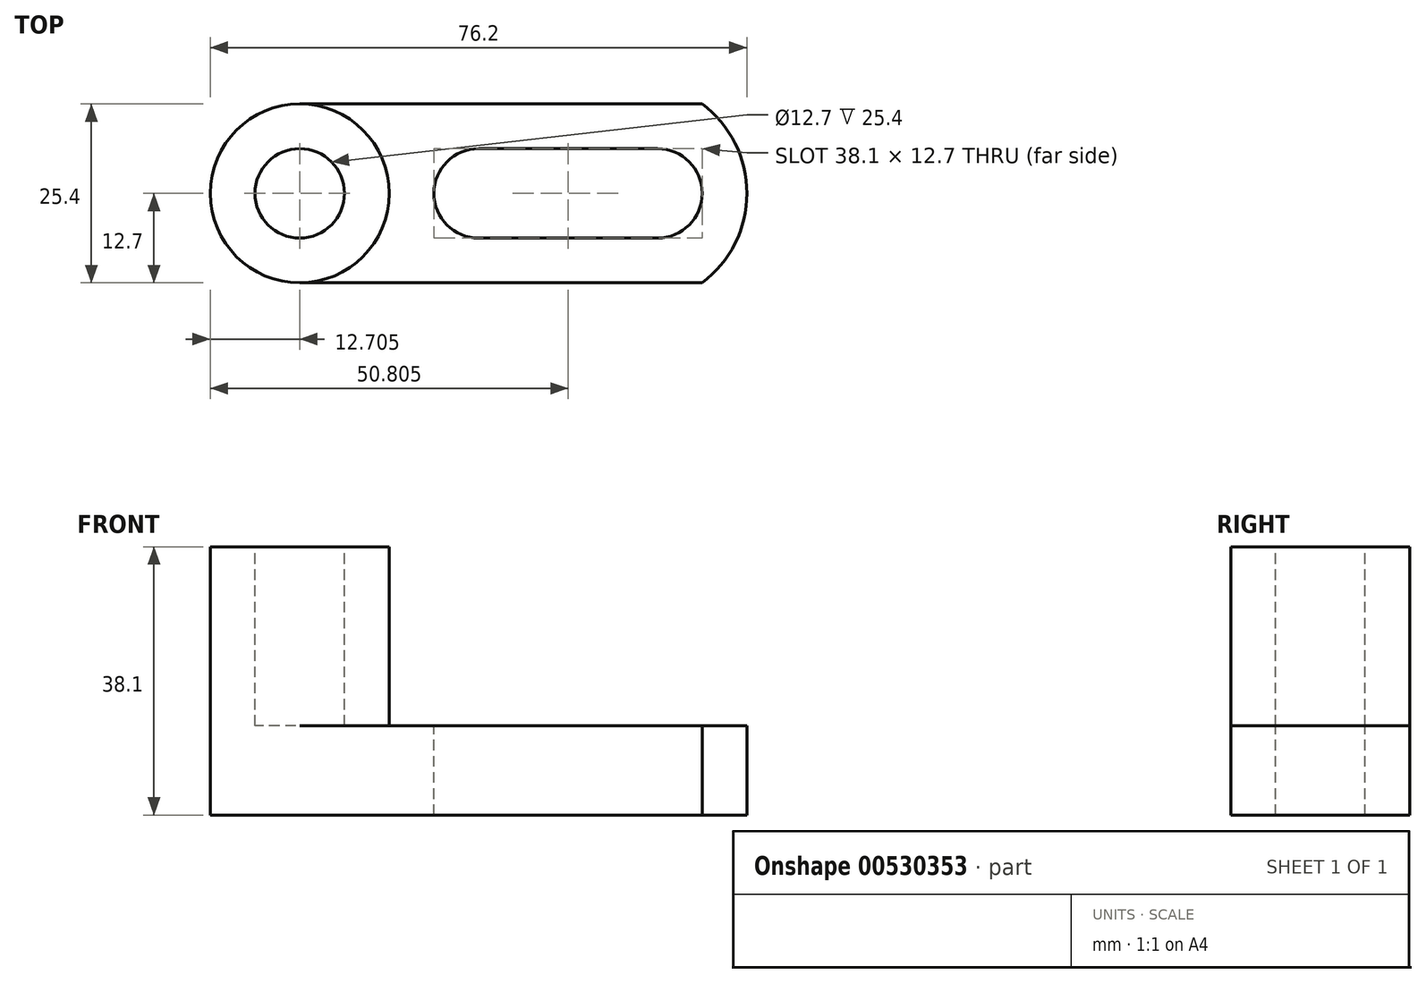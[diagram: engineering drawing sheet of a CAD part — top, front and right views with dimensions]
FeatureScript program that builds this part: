
annotation { "Feature Type Name" : "Feature", "Feature Type Description" : "" }
export const myFeature = defineFeature(function(context is Context, id is Id, definition is map)
    precondition{}
    {
        {
            var Q0;
            Q0=qCreatedBy(makeId("Front.planeOp"),FACE);
            var sketch = newSketch(context, id + "F0", { "sketchPlane" : qUnion([Q0])});
            skLineSegment(sketch, "E0", {"start": v(-50.57, 38.1) * mm, "end": v(-50.57, 0) * mm});
            skLineSegment(sketch, "E1", {"start": v(-50.57, 0) * mm, "end": v(25.63, 0) * mm});
            skLineSegment(sketch, "E2", {"start": v(25.63, 0) * mm, "end": v(25.63, 12.7) * mm});
            skLineSegment(sketch, "E3", {"start": v(25.63, 12.7) * mm, "end": v(-25.17, 12.7) * mm});
            skLineSegment(sketch, "E4", {"start": v(-25.17, 12.7) * mm, "end": v(-25.17, 38.1) * mm});
            skLineSegment(sketch, "E5", {"start": v(-25.17, 38.1) * mm, "end": v(-50.57, 38.1) * mm});
            skSolve(sketch);
        }
        {
            var Q0;
            Q0 = qSketchRegion(id + "F0", true);
            extrude(context, id + "F1", {"entities" : qUnion([Q0]), "depth" : 25.4 * mm, "offsetDistance" : 25.4 * mm});
        }
        {
            var Q0;
            Q0=makeQuery(id+"F1.opExtrude","SWEPT_FACE",FACE,{"disambiguationData":[OSD([sQuery(id+"F0.wireOp",EDGE,"E5")])]});
            var sketch = newSketch(context, id + "F2", { "sketchPlane" : qUnion([Q0])});
            skSolve(sketch);
        }
        {
            var Q0;
            {var subQ0=sQuery(id+"F0.wireOp",EDGE,"E5");Q0=makeQuery(id+"F2.imprint","IMPRINT",FACE,{"disambiguationData":[TD([[makeQuery(id+"F2.imprint","IMPRINT",EDGE,{"derivedFrom":makeQuery(id+"F1.opExtrude","CAP_EDGE",EDGE,{"disambiguationData":[OSD([subQ0])],"isStart":true})}),1.0]])]});}
            var sketch = newSketch(context, id + "F3", { "sketchPlane" : qUnion([Q0])});
            skCircle(sketch, "E6", {"center": v(-37.87, -12.7) * mm, "radius": 12.7 * mm});
            skSolve(sketch);
        }
        {
            var Q0;
            {var subQ0=sQuery(id+"F3.wireOp",EDGE,"E6");var subQ1=sQuery(id+"F0.wireOp",EDGE,"E5");var subQ2=makeQuery(id+"F2.imprint","IMPRINT",EDGE,{"derivedFrom":makeQuery(id+"F1.opExtrude","CAP_EDGE",EDGE,{"disambiguationData":[OSD([subQ1])],"isStart":true})});var subQ3=makeQuery(id+"F3.imprint","INTERSECT",VERTEX,{"derivedFrom":[subQ2,subQ0]});Q0=makeQuery(id+"F3.imprint","IMPRINT",FACE,{"disambiguationData":[TD([[makeQuery(id+"F3.imprint","IMPRINT",EDGE,{"disambiguationData":[TD([[subQ3,-1.0]])],"derivedFrom":subQ0}),-1.0]])]});}
            var Q1;
            {var subQ0=sQuery(id+"F3.wireOp",EDGE,"E6");var subQ1=sQuery(id+"F0.wireOp",EDGE,"E5");var subQ2=makeQuery(id+"F2.imprint","IMPRINT",EDGE,{"derivedFrom":makeQuery(id+"F1.opExtrude","CAP_EDGE",EDGE,{"disambiguationData":[OSD([subQ1])],"isStart":true})});var subQ3=makeQuery(id+"F3.imprint","INTERSECT",VERTEX,{"derivedFrom":[subQ2,subQ0]});Q1=makeQuery(id+"F3.imprint","IMPRINT",FACE,{"disambiguationData":[TD([[makeQuery(id+"F3.imprint","IMPRINT",EDGE,{"disambiguationData":[TD([[subQ3,1.0]])],"derivedFrom":subQ0}),-1.0]])]});}
            var Q2;
            {var subQ0=sQuery(id+"F3.wireOp",EDGE,"E6");var subQ1=sQuery(id+"F0.wireOp",EDGE,"E5");var subQ4=makeQuery(id+"F2.imprint","IMPRINT",EDGE,{"derivedFrom":makeQuery(id+"F1.opExtrude","CAP_EDGE",EDGE,{"disambiguationData":[OSD([subQ1])],"isStart":false})});var subQ5=makeQuery(id+"F3.imprint","INTERSECT",VERTEX,{"derivedFrom":[subQ4,subQ0]});Q2=makeQuery(id+"F3.imprint","IMPRINT",FACE,{"disambiguationData":[TD([[makeQuery(id+"F3.imprint","IMPRINT",EDGE,{"disambiguationData":[TD([[subQ5,1.0]])],"derivedFrom":subQ0}),-1.0]])]});}
            var Q3;
            {var subQ0=sQuery(id+"F3.wireOp",EDGE,"E6");var subQ1=sQuery(id+"F0.wireOp",EDGE,"E5");var subQ4=makeQuery(id+"F2.imprint","IMPRINT",EDGE,{"derivedFrom":makeQuery(id+"F1.opExtrude","CAP_EDGE",EDGE,{"disambiguationData":[OSD([subQ1])],"isStart":false})});var subQ5=makeQuery(id+"F3.imprint","INTERSECT",VERTEX,{"derivedFrom":[subQ4,subQ0]});Q3=makeQuery(id+"F3.imprint","IMPRINT",FACE,{"disambiguationData":[TD([[makeQuery(id+"F3.imprint","IMPRINT",EDGE,{"disambiguationData":[TD([[subQ5,-1.0]])],"derivedFrom":subQ0}),-1.0]])]});}
            extrude(context, id + "F4", {"entities" : qUnion([Q0, Q1, Q2, Q3]), "operationType" : NewBodyOperationType.REMOVE, "oppositeDirection" : true, "depth" : 25.4 * mm, "offsetDistance" : 25.4 * mm});
        }
        {
            var Q0;
            {var subQ0=sQuery(id+"F0.wireOp",EDGE,"E5");var subQ1=makeQuery(id+"F2.imprint","IMPRINT",EDGE,{"derivedFrom":makeQuery(id+"F1.opExtrude","CAP_EDGE",EDGE,{"disambiguationData":[OSD([subQ0])],"isStart":false})});var subQ2=sQuery(id+"F0.wireOp",EDGE,"E0");var subQ3=makeQuery(id+"F2.imprint","IMPRINT",EDGE,{"derivedFrom":makeQuery(id+"F1.opExtrude","SWEPT_EDGE",EDGE,{"disambiguationData":[OSD([subQ2,subQ0])]})});var subQ4=makeQuery(id+"F3.imprint","INTERSECT",VERTEX,{"derivedFrom":[subQ3,subQ1]});var subQ5=sQuery(id+"F3.wireOp",EDGE,"E6");var subQ6=makeQuery(id+"F3.imprint","INTERSECT",VERTEX,{"derivedFrom":[subQ1,subQ5]});Q0=makeQuery(id+"F4.boolean.opBoolean","COPY",FACE,{"derivedFrom":makeQuery(id+"F4.opExtrude","CAP_FACE",FACE,{"disambiguationData":[OSD([subQ2,subQ0,subQ5]),TDD([makeQuery(id+"F3.imprint","IMPRINT",EDGE,{"disambiguationData":[TD([[subQ6,1.0]])],"derivedFrom":subQ5}),makeQuery(id+"F3.imprint","IMPRINT",EDGE,{"disambiguationData":[TD([[subQ4,-1.0]])],"derivedFrom":subQ3}),makeQuery(id+"F3.imprint","IMPRINT",EDGE,{"disambiguationData":[TD([[subQ6,-1.0]])],"derivedFrom":subQ1})])],"isStart":false})});}
            extrude(context, id + "F5", {"entities" : qUnion([Q0]), "operationType" : NewBodyOperationType.REMOVE, "endBound" : BoundingType.THROUGH_ALL, "oppositeDirection" : true, "depth" : 25.4 * mm, "offsetDistance" : 25.4 * mm});
        }
        {
            var Q0;
            {var subQ0=sQuery(id+"F0.wireOp",EDGE,"E5");var subQ1=makeQuery(id+"F2.imprint","IMPRINT",EDGE,{"derivedFrom":makeQuery(id+"F1.opExtrude","CAP_EDGE",EDGE,{"disambiguationData":[OSD([subQ0])],"isStart":true})});var subQ2=sQuery(id+"F0.wireOp",EDGE,"E0");var subQ3=makeQuery(id+"F2.imprint","IMPRINT",EDGE,{"derivedFrom":makeQuery(id+"F1.opExtrude","SWEPT_EDGE",EDGE,{"disambiguationData":[OSD([subQ2,subQ0])]})});var subQ4=makeQuery(id+"F3.imprint","INTERSECT",VERTEX,{"derivedFrom":[subQ3,subQ1]});var subQ5=sQuery(id+"F3.wireOp",EDGE,"E6");var subQ6=makeQuery(id+"F3.imprint","INTERSECT",VERTEX,{"derivedFrom":[subQ1,subQ5]});Q0=makeQuery(id+"F4.boolean.opBoolean","COPY",FACE,{"derivedFrom":makeQuery(id+"F4.opExtrude","CAP_FACE",FACE,{"disambiguationData":[OSD([subQ2,subQ0,subQ5]),TDD([makeQuery(id+"F3.imprint","IMPRINT",EDGE,{"disambiguationData":[TD([[subQ6,-1.0]])],"derivedFrom":subQ5}),makeQuery(id+"F3.imprint","IMPRINT",EDGE,{"disambiguationData":[TD([[subQ4,1.0]])],"derivedFrom":subQ3}),makeQuery(id+"F3.imprint","IMPRINT",EDGE,{"disambiguationData":[TD([[subQ6,-1.0]])],"derivedFrom":subQ1})])],"isStart":false})});}
            extrude(context, id + "F6", {"entities" : qUnion([Q0]), "operationType" : NewBodyOperationType.REMOVE, "endBound" : BoundingType.THROUGH_ALL, "oppositeDirection" : true, "depth" : 25.4 * mm, "offsetDistance" : 25.4 * mm});
        }
        {
            var Q0;
            {var subQ0=sQuery(id+"F0.wireOp",EDGE,"E5");Q0=makeQuery(id+"F2.imprint","IMPRINT",FACE,{"disambiguationData":[TD([[makeQuery(id+"F2.imprint","IMPRINT",EDGE,{"derivedFrom":makeQuery(id+"F1.opExtrude","CAP_EDGE",EDGE,{"disambiguationData":[OSD([subQ0])],"isStart":true})}),1.0]])]});}
            var sketch = newSketch(context, id + "F7", { "sketchPlane" : qUnion([Q0])});
            skCircle(sketch, "E7", {"center": v(-37.87, -12.7) * mm, "radius": 6.35 * mm});
            skSolve(sketch);
        }
        {
            var Q0;
            Q0 = qSketchRegion(id + "F7", true);
            extrude(context, id + "F8", {"entities" : qUnion([Q0]), "operationType" : NewBodyOperationType.REMOVE, "oppositeDirection" : true, "depth" : 25.4 * mm, "offsetDistance" : 25.4 * mm});
        }
        {
            var Q0;
            {var subQ0=sQuery(id+"F0.wireOp",EDGE,"E5");var subQ1=makeQuery(id+"F2.imprint","IMPRINT",EDGE,{"derivedFrom":makeQuery(id+"F1.opExtrude","CAP_EDGE",EDGE,{"disambiguationData":[OSD([subQ0])],"isStart":false})});var subQ2=sQuery(id+"F0.wireOp",EDGE,"E4");var subQ3=makeQuery(id+"F2.imprint","IMPRINT",EDGE,{"derivedFrom":makeQuery(id+"F1.opExtrude","SWEPT_EDGE",EDGE,{"disambiguationData":[OSD([subQ2,subQ0])]})});var subQ4=makeQuery(id+"F3.imprint","INTERSECT",VERTEX,{"derivedFrom":[subQ3,subQ1]});var subQ5=sQuery(id+"F3.wireOp",EDGE,"E6");var subQ6=makeQuery(id+"F3.imprint","INTERSECT",VERTEX,{"derivedFrom":[subQ1,subQ5]});var subQ8=makeQuery(id+"F2.imprint","IMPRINT",EDGE,{"derivedFrom":makeQuery(id+"F1.opExtrude","CAP_EDGE",EDGE,{"disambiguationData":[OSD([subQ0])],"isStart":true})});var subQ9=makeQuery(id+"F3.imprint","INTERSECT",VERTEX,{"derivedFrom":[subQ3,subQ8]});var subQ10=makeQuery(id+"F3.imprint","INTERSECT",VERTEX,{"derivedFrom":[subQ8,subQ5]});Q0=makeQuery(id+"F4.boolean.opBoolean","MERGE",FACE,{"derivedFrom":[makeQuery(id+"F1.opExtrude","SWEPT_FACE",FACE,{"disambiguationData":[OSD([sQuery(id+"F0.wireOp",EDGE,"E3")])]}),makeQuery(id+"F4.opExtrude","CAP_FACE",FACE,{"disambiguationData":[OSD([subQ2,subQ0,subQ5]),TDD([makeQuery(id+"F3.imprint","IMPRINT",EDGE,{"disambiguationData":[TD([[subQ10,1.0]])],"derivedFrom":subQ5}),makeQuery(id+"F3.imprint","IMPRINT",EDGE,{"disambiguationData":[TD([[subQ9,1.0]])],"derivedFrom":subQ3}),makeQuery(id+"F3.imprint","IMPRINT",EDGE,{"disambiguationData":[TD([[subQ10,1.0]])],"derivedFrom":subQ8})])],"isStart":false}),makeQuery(id+"F4.opExtrude","CAP_FACE",FACE,{"disambiguationData":[OSD([subQ2,subQ0,subQ5]),TDD([makeQuery(id+"F3.imprint","IMPRINT",EDGE,{"disambiguationData":[TD([[subQ6,-1.0]])],"derivedFrom":subQ5}),makeQuery(id+"F3.imprint","IMPRINT",EDGE,{"disambiguationData":[TD([[subQ4,-1.0]])],"derivedFrom":subQ3}),makeQuery(id+"F3.imprint","IMPRINT",EDGE,{"disambiguationData":[TD([[subQ6,1.0]])],"derivedFrom":subQ1})])],"isStart":false})]});}
            var sketch = newSketch(context, id + "F9", { "sketchPlane" : qUnion([Q0])});
            skCircle(sketch, "E8", {"center": v(-12.47, -12.7) * mm, "radius": 6.35 * mm});
            skPoint(sketch, "E8.centerSnap0", {"position": v(-25.17, -12.7) * mm});
            skCircle(sketch, "E9", {"center": v(12.93, -12.7) * mm, "radius": 6.35 * mm});
            skLineSegment(sketch, "E10", {"start": v(-12.47, -19.05) * mm, "end": v(12.93, -19.05) * mm});
            skLineSegment(sketch, "E11", {"start": v(-12.47, -6.35) * mm, "end": v(12.93, -6.35) * mm});
            skSolve(sketch);
        }
        {
            var Q0;
            Q0 = qSketchRegion(id + "F9", true);
            extrude(context, id + "F10", {"entities" : qUnion([Q0]), "operationType" : NewBodyOperationType.REMOVE, "endBound" : BoundingType.THROUGH_ALL, "oppositeDirection" : true, "depth" : 25.4 * mm, "offsetDistance" : 25.4 * mm});
        }
        {
            var Q0;
            {var subQ0=sQuery(id+"F0.wireOp",EDGE,"E5");var subQ1=makeQuery(id+"F2.imprint","IMPRINT",EDGE,{"derivedFrom":makeQuery(id+"F1.opExtrude","CAP_EDGE",EDGE,{"disambiguationData":[OSD([subQ0])],"isStart":false})});var subQ2=sQuery(id+"F0.wireOp",EDGE,"E4");var subQ3=makeQuery(id+"F2.imprint","IMPRINT",EDGE,{"derivedFrom":makeQuery(id+"F1.opExtrude","SWEPT_EDGE",EDGE,{"disambiguationData":[OSD([subQ2,subQ0])]})});var subQ4=makeQuery(id+"F3.imprint","INTERSECT",VERTEX,{"derivedFrom":[subQ3,subQ1]});var subQ5=sQuery(id+"F3.wireOp",EDGE,"E6");var subQ6=makeQuery(id+"F3.imprint","INTERSECT",VERTEX,{"derivedFrom":[subQ1,subQ5]});var subQ8=makeQuery(id+"F2.imprint","IMPRINT",EDGE,{"derivedFrom":makeQuery(id+"F1.opExtrude","CAP_EDGE",EDGE,{"disambiguationData":[OSD([subQ0])],"isStart":true})});var subQ9=makeQuery(id+"F3.imprint","INTERSECT",VERTEX,{"derivedFrom":[subQ3,subQ8]});var subQ10=makeQuery(id+"F3.imprint","INTERSECT",VERTEX,{"derivedFrom":[subQ8,subQ5]});Q0=makeQuery(id+"F4.boolean.opBoolean","MERGE",FACE,{"derivedFrom":[makeQuery(id+"F1.opExtrude","SWEPT_FACE",FACE,{"disambiguationData":[OSD([sQuery(id+"F0.wireOp",EDGE,"E3")])]}),makeQuery(id+"F4.opExtrude","CAP_FACE",FACE,{"disambiguationData":[OSD([subQ2,subQ0,subQ5]),TDD([makeQuery(id+"F3.imprint","IMPRINT",EDGE,{"disambiguationData":[TD([[subQ10,1.0]])],"derivedFrom":subQ5}),makeQuery(id+"F3.imprint","IMPRINT",EDGE,{"disambiguationData":[TD([[subQ9,1.0]])],"derivedFrom":subQ3}),makeQuery(id+"F3.imprint","IMPRINT",EDGE,{"disambiguationData":[TD([[subQ10,1.0]])],"derivedFrom":subQ8})])],"isStart":false}),makeQuery(id+"F4.opExtrude","CAP_FACE",FACE,{"disambiguationData":[OSD([subQ2,subQ0,subQ5]),TDD([makeQuery(id+"F3.imprint","IMPRINT",EDGE,{"disambiguationData":[TD([[subQ6,-1.0]])],"derivedFrom":subQ5}),makeQuery(id+"F3.imprint","IMPRINT",EDGE,{"disambiguationData":[TD([[subQ4,-1.0]])],"derivedFrom":subQ3}),makeQuery(id+"F3.imprint","IMPRINT",EDGE,{"disambiguationData":[TD([[subQ6,1.0]])],"derivedFrom":subQ1})])],"isStart":false})]});}
            var sketch = newSketch(context, id + "F11", { "sketchPlane" : qUnion([Q0])});
            skArc(sketch, "E12", {"start": v(19.28, -25.4) * mm, "mid": v(25.63, -12.7) * mm, "end": v(19.28, 0) * mm});
            skSolve(sketch);
        }
        {
            var Q0;
            Q0 = qSketchRegion(id + "F11", true);
            var Q1;
            {var subQ0=sQuery(id+"F11.wireOp",EDGE,"E12");var subQ3=sQuery(id+"F0.wireOp",EDGE,"E3");var subQ6=makeQuery(id+"F1.opExtrude","SWEPT_EDGE",EDGE,{"disambiguationData":[OSD([sQuery(id+"F0.wireOp",EDGE,"E2"),subQ3])]});var subQ7=makeQuery(id+"F11.imprint","INTERSECT",VERTEX,{"derivedFrom":[subQ6,subQ0]});Q1=makeQuery(id+"F11.imprint","IMPRINT",FACE,{"disambiguationData":[TD([[makeQuery(id+"F11.imprint","IMPRINT",EDGE,{"disambiguationData":[TD([[subQ7,-1.0]])],"derivedFrom":subQ0}),-1.0]])]});}
            var Q2;
            {var subQ0=sQuery(id+"F11.wireOp",EDGE,"E12");var subQ3=sQuery(id+"F0.wireOp",EDGE,"E3");var subQ6=makeQuery(id+"F1.opExtrude","SWEPT_EDGE",EDGE,{"disambiguationData":[OSD([sQuery(id+"F0.wireOp",EDGE,"E2"),subQ3])]});var subQ7=makeQuery(id+"F11.imprint","INTERSECT",VERTEX,{"derivedFrom":[subQ6,subQ0]});Q2=makeQuery(id+"F11.imprint","IMPRINT",FACE,{"disambiguationData":[TD([[makeQuery(id+"F11.imprint","IMPRINT",EDGE,{"disambiguationData":[TD([[subQ7,1.0]])],"derivedFrom":subQ0}),-1.0]])]});}
            extrude(context, id + "F12", {"entities" : qUnion([Q0, Q1, Q2]), "operationType" : NewBodyOperationType.REMOVE, "endBound" : BoundingType.THROUGH_ALL, "oppositeDirection" : true, "depth" : 25.4 * mm, "offsetDistance" : 25.4 * mm});
        }
    });
